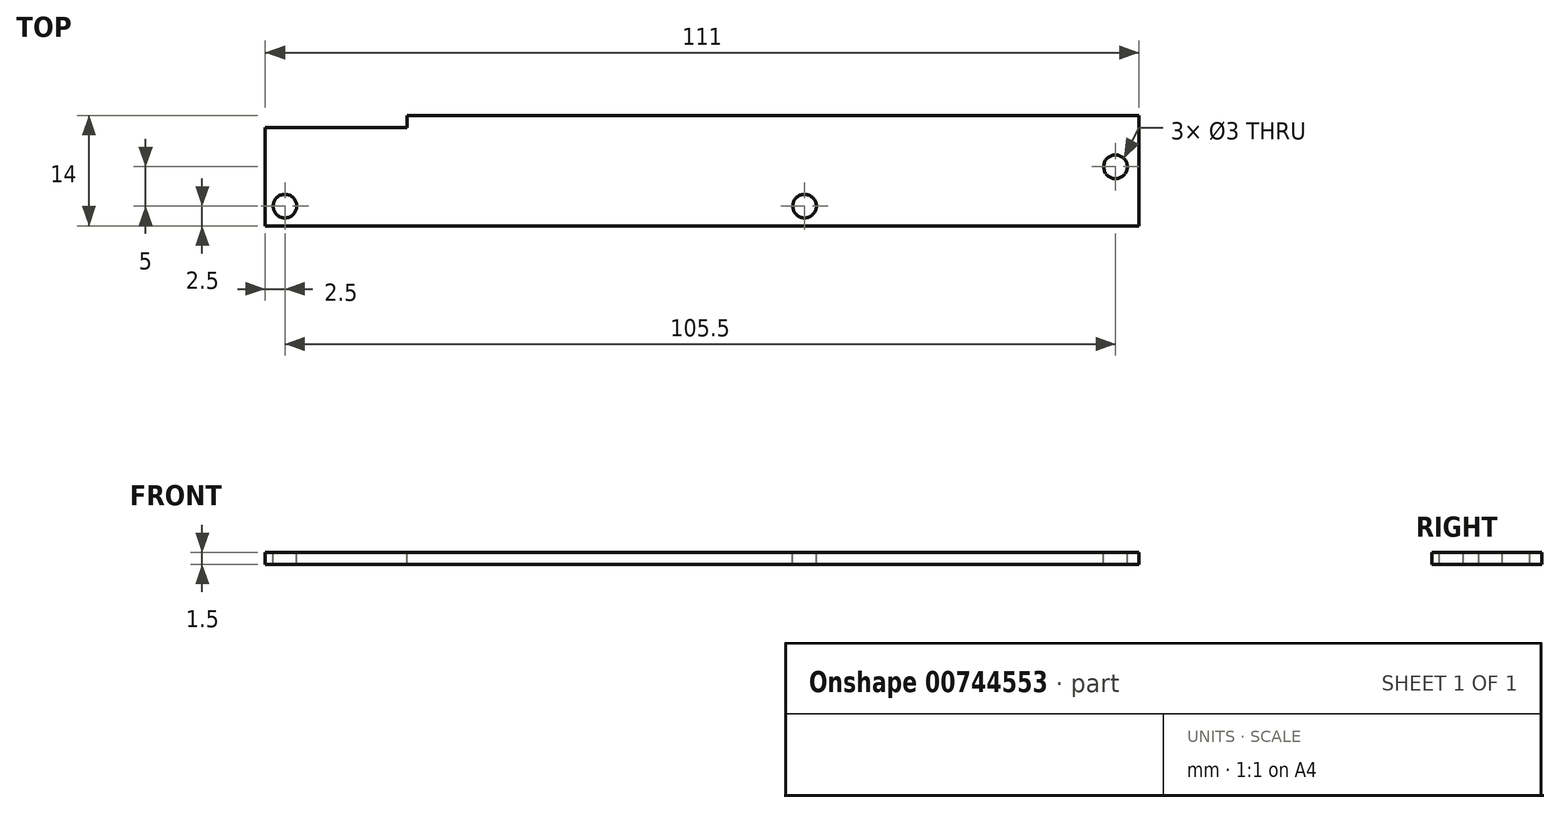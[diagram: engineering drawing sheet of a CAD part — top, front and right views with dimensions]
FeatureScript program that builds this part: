
annotation { "Feature Type Name" : "Feature", "Feature Type Description" : "" }
export const myFeature = defineFeature(function(context is Context, id is Id, definition is map)
    precondition{}
    {
        {
            var Q0;
            Q0=qCreatedBy(makeId("Top.planeOp"),FACE);
            var sketch = newSketch(context, id + "F0", { "sketchPlane" : qUnion([Q0])});
            skLineSegment(sketch, "E0.bottom", {"start": v(-55.5, -7) * mm, "end": v(55.5, -7) * mm});
            skLineSegment(sketch, "E0.top", {"start": v(-55.5, 7) * mm, "end": v(55.5, 7) * mm});
            skLineSegment(sketch, "E0.left", {"start": v(-55.5, -7) * mm, "end": v(-55.5, 7) * mm});
            skLineSegment(sketch, "E0.right", {"start": v(55.5, -7) * mm, "end": v(55.5, 7) * mm});
            skLineSegment(sketch, "E1", {"start": v(0, -54.13) * mm, "end": v(0, 92.6) * mm, "construction": true});
            skLineSegment(sketch, "E2", {"start": v(-84.63, 0) * mm, "end": v(111.85, 0) * mm, "construction": true});
            skLineSegment(sketch, "E3.bottom", {"start": v(-55.5, 7) * mm, "end": v(-37.5, 7) * mm});
            skLineSegment(sketch, "E3.top", {"start": v(-55.5, 5.5) * mm, "end": v(-37.5, 5.5) * mm});
            skLineSegment(sketch, "E3.left", {"start": v(-55.5, 7) * mm, "end": v(-55.5, 5.5) * mm});
            skLineSegment(sketch, "E3.right", {"start": v(-37.5, 7) * mm, "end": v(-37.5, 5.5) * mm});
            skCircle(sketch, "E4", {"center": v(-53, -4.5) * mm, "radius": 1.5 * mm});
            skCircle(sketch, "E5", {"center": v(13, -4.5) * mm, "radius": 1.5 * mm});
            skCircle(sketch, "E6", {"center": v(52.5, 0.5) * mm, "radius": 1.5 * mm});
            skSolve(sketch);
        }
        {
            var Q0;
            Q0=makeQuery(id+"F0.imprint","IMPRINT",FACE,{"disambiguationData":[TD([[makeQuery(id+"F0.imprint","IMPRINT",EDGE,{"derivedFrom":sQuery(id+"F0.wireOp",EDGE,"E0.bottom")}),1.0]])]});
            extrude(context, id + "F1", {"entities" : qUnion([Q0]), "oppositeDirection" : true, "depth" : 1.5 * mm, "offsetDistance" : 25 * mm});
        }
    });
